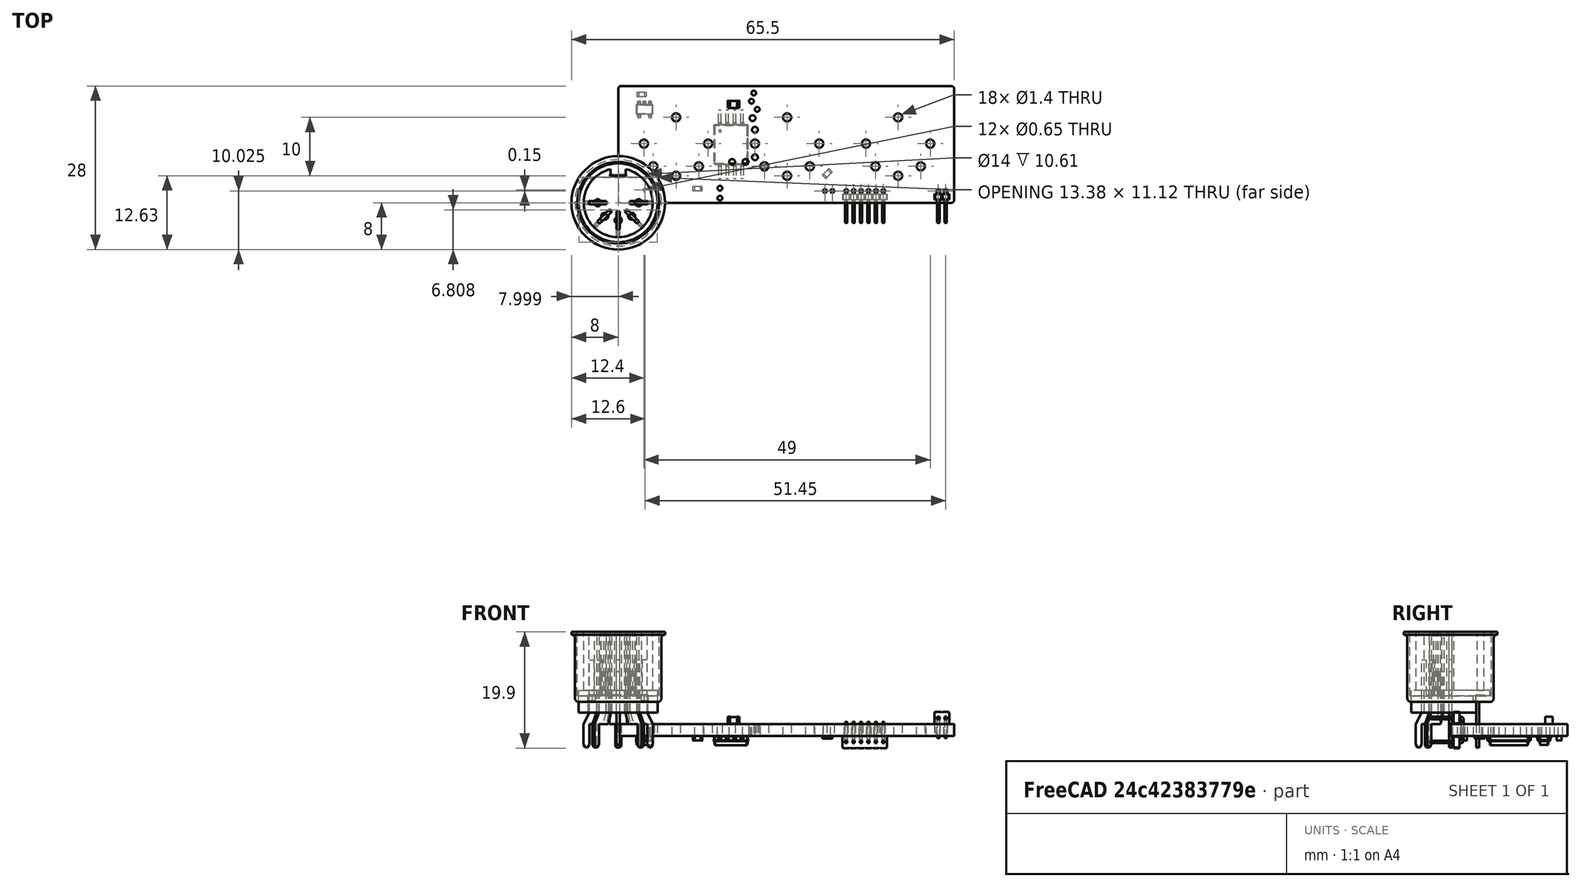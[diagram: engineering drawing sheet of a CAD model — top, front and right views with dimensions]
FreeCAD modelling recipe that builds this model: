
FCSTD DOCUMENT  (FreeCAD 0.20R29177 (Git))
Label: Ultra-midi1
License: All rights reserved
LicenseURL: http://en.wikipedia.org/wiki/All_rights_reserved
objects: Part::Feature×31, App::Link×16, App::Part×8, PartDesign::CoordinateSystem×1, Sketcher::SketchObject×1
note: 33 computed .brp shape members not serialized (recipe doc carries the construction recipe); baked Part::Feature solids carry a one-line shape summary decoded from their .brp

FEATURE [PartDesign::CoordinateSystem] Local_CS_69dd
  AttacherType = Attacher::AttachEngine3D
FEATURE [Part::Feature] Pcb_69dd
  Placement = pos=(-116,98,0) rot=(0,0,1;0rad)
  shape: bbox 57.5 x 20 x 2 mm, 50 faces (baked)
FEATURE [Sketcher::SketchObject] PCB_Sketch_69dd
  FullyConstrained = false
  sketch-geometry (18):
    g0: LineSegment StartX=57 StartY=20 StartZ=0 EndX=0.5 EndY=20 EndZ=0
    g1: LineSegment StartX=8e-16 StartY=19.5 StartZ=0 EndX=0 EndY=0.5 EndZ=0
    g2: LineSegment StartX=57.5 StartY=0.5 StartZ=0 EndX=57.5 EndY=19.5 EndZ=0
    g3: LineSegment StartX=0.5 StartY=0 StartZ=0 EndX=57 EndY=-1.3e-15 EndZ=0
    g4: ArcOfCircle CenterX=57 CenterY=0.500001 CenterZ=0 NormalX=0 NormalY=0 NormalZ=-1 AngleXU=-3.14159 Radius=0.500001 StartAngle=0 EndAngle=1.57079
    g5: ArcOfCircle CenterX=0.500001 CenterY=19.5 CenterZ=0 NormalX=0 NormalY=0 NormalZ=-1 AngleXU=2.66714e-06 Radius=0.500001 StartAngle=0 EndAngle=1.57079
    g6: ArcOfCircle CenterX=0.500001 CenterY=0.500001 CenterZ=0 NormalX=0 NormalY=0 NormalZ=-1 AngleXU=-1.57079 Radius=0.500001 StartAngle=0 EndAngle=1.57079
    g7: ArcOfCircle CenterX=57 CenterY=19.5 CenterZ=0 NormalX=0 NormalY=0 NormalZ=-1 AngleXU=1.5708 Radius=0.500001 StartAngle=0 EndAngle=1.57079
    g8: Circle CenterX=19.5 CenterY=7 CenterZ=0 NormalX=0 NormalY=0 NormalZ=1 AngleXU=0 Radius=0.5
    g9: Circle CenterX=17.4 CenterY=2.5 CenterZ=0 NormalX=0 NormalY=0 NormalZ=1 AngleXU=0 Radius=0.4
    g10: Circle CenterX=23.4 CenterY=7.8 CenterZ=0 NormalX=0 NormalY=0 NormalZ=1 AngleXU=0 Radius=0.5
    g11: Circle CenterX=23.2 CenterY=18.8 CenterZ=0 NormalX=0 NormalY=0 NormalZ=1 AngleXU=0 Radius=0.4
    g12: Circle CenterX=22.8 CenterY=17.4 CenterZ=0 NormalX=0 NormalY=0 NormalZ=1 AngleXU=0 Radius=0.4
    g13: Circle CenterX=23 CenterY=14.5 CenterZ=0 NormalX=0 NormalY=0 NormalZ=1 AngleXU=0 Radius=0.5
    g14: Circle CenterX=23.4 CenterY=12.5 CenterZ=0 NormalX=0 NormalY=0 NormalZ=1 AngleXU=0 Radius=0.5
    g15: Circle CenterX=17.4 CenterY=0.8 CenterZ=0 NormalX=0 NormalY=0 NormalZ=1 AngleXU=0 Radius=0.4
    g16: Circle CenterX=23.8 CenterY=16 CenterZ=0 NormalX=0 NormalY=0 NormalZ=1 AngleXU=0 Radius=0.4
    g17: Circle CenterX=21.8 CenterY=7 CenterZ=0 NormalX=0 NormalY=0 NormalZ=1 AngleXU=0 Radius=0.5
  constraints (8):
    c: Coincident(g1,g6)
    c: Coincident(g1,g5)
    c: Coincident(g3,g6)
    c: Coincident(g0,g5)
    c: Coincident(g3,g4)
    c: Coincident(g0,g7)
    c: Coincident(g2,g4)
    c: Coincident(g2,g7)
FEATURE [Part::Feature] Shape  label="J2_PinHeader_1x02_P127mm_Horizontal_337eb045ee12"
  Placement = pos=(56.05,2.025,0) rot=(0,0,-1;1.5708rad)
  shape: bbox 2.54 x 5.7 x 4.5 mm, 58 faces (baked)
FEATURE [Part::Feature] Shape001  label="C6_C_0805_2012Metric_c09b5ff471bc"
  Placement = pos=(19.75,16.85,0) rot=(0,0,1;0rad)
  shape: bbox 2 x 1.25 x 1.25 mm, 28 faces (baked)
FEATURE [App::Link] J2_PinHeader_1x02_P127mm_Horizontal_337eb045ee12_ln_  label="J3_PinHeader_1x02_P127mm_Horizontal_27ee44c8c3d4"
  LinkPlacement = pos=(36.65,2.025,0) rot=(0,0,-1;1.5708rad)
  LinkedObject = -> Shape
  Placement = pos=(36.65,2.025,0) rot=(0,0,-1;1.5708rad)
FEATURE [Part::Feature] Shape002  label="FB3_L_0603_1608Metric_df2c29076625"
  Placement = pos=(13.6,2.4,-2) rot=(0,1,0;3.14159rad)
  shape: bbox 1.6 x 0.8 x 0.8 mm, 28 faces (baked)
FEATURE [Part::Feature] Shape003  label="C5_C_0603_1608Metric_0867c8c5745e"
  Placement = pos=(4,18.6,-2) rot=(1,0,0;3.14159rad)
  shape: bbox 1.6 x 0.8 x 0.8 mm, 28 faces (baked)
FEATURE [Part::Feature] Shape004  label="R5_R_0603_1608Metric_8c8bab43711c"
  Placement = pos=(35.8,5,-2) rot=(0.92388,0.382683,0;3.14159rad)
  shape: bbox 1.697 x 1.697 x 0.45 mm, 26 faces (baked)
FEATURE [Part::Feature] Shape005  label="J4_PinHeader_1x06_P127mm_Horizontal_489f8f595e1f"
  Placement = pos=(39.025,2.025,-2) rot=(0.707107,-0.707107,0;3.14159rad)
  shape: bbox 7.62 x 5.7 x 4.5 mm, 166 faces (baked)
FEATURE [App::Link] FB3_L_0603_1608Metric_df2c29076625_ln_  label="FB1_L_0603_1608Metric_149065dd4c7b"
  LinkPlacement = pos=(36,7.4,-2) rot=(0.92388,0.382683,0;3.14159rad)
  LinkedObject = -> Shape002
  Placement = pos=(36,7.4,-2) rot=(0.92388,0.382683,0;3.14159rad)
FEATURE [Part::Feature] Shape006  label="U1_SSO_8_68x59mm_P127mm_Clearance8mm_cd01ce0f9bbe"
  Placement = pos=(19.3,10,-2) rot=(0.707107,-0.707107,0;3.14159rad)
  shape: bbox 5.9 x 11.7 x 1.6 mm, 156 faces (baked)
FEATURE [Part::Feature] Shape007  label="U2_SOT_23_5_2942c334eb8a"
  Placement = pos=(4.5,16,-2) rot=(0.707107,-0.707107,0;3.14159rad)
  shape: bbox 2.9 x 2.8 x 1.55 mm, 109 faces (baked)
FEATURE [App::Link] R5_R_0603_1608Metric_8c8bab43711c_ln_  label="R4_R_0603_1608Metric_3ff6b89587b2"
  LinkPlacement = pos=(8,10,-2) rot=(0.707107,0.707107,0;3.14159rad)
  LinkedObject = -> Shape004
  Placement = pos=(8,10,-2) rot=(0.707107,0.707107,0;3.14159rad)
FEATURE [App::Link] C5_C_0603_1608Metric_0867c8c5745e_ln_  label="C2_C_0603_1608Metric_22715801060e"
  LinkPlacement = pos=(10.8,8.2,-2) rot=(1,0,0;3.14159rad)
  LinkedObject = -> Shape003
  Placement = pos=(10.8,8.2,-2) rot=(1,0,0;3.14159rad)
FEATURE [App::Link] C6_C_0805_2012Metric_c09b5ff471bc_ln_  label="C4_C_0805_2012Metric_26a949b8cd84"
  LinkPlacement = pos=(7,12.5,-2) rot=(0,1,0;3.14159rad)
  LinkedObject = -> Shape001
  Placement = pos=(7,12.5,-2) rot=(0,1,0;3.14159rad)
FEATURE [App::Link] R5_R_0603_1608Metric_8c8bab43711c_ln_001  label="R2_R_0603_1608Metric_4e10fd813094"
  LinkPlacement = pos=(49.4,16.5,-2) rot=(0.92388,-0.382683,0;3.14159rad)
  LinkedObject = -> Shape004
  Placement = pos=(49.4,16.5,-2) rot=(0.92388,-0.382683,0;3.14159rad)
FEATURE [App::Link] FB3_L_0603_1608Metric_df2c29076625_ln_001  label="FB2_L_0603_1608Metric_fe7989b07d85"
  LinkPlacement = pos=(12.8,12.2,-2) rot=(0.707107,0.707107,0;3.14159rad)
  LinkedObject = -> Shape002
  Placement = pos=(12.8,12.2,-2) rot=(0.707107,0.707107,0;3.14159rad)
FEATURE [App::Link] C5_C_0603_1608Metric_0867c8c5745e_ln_001  label="C1_C_0603_1608Metric_b41121d6c93c"
  LinkPlacement = pos=(46.1,16.3,-2) rot=(0.92388,0.382683,0;3.14159rad)
  LinkedObject = -> Shape003
  Placement = pos=(46.1,16.3,-2) rot=(0.92388,0.382683,0;3.14159rad)
FEATURE [App::Link] R5_R_0603_1608Metric_8c8bab43711c_ln_002  label="R7_R_0603_1608Metric_dfa80113c302"
  LinkPlacement = pos=(27,1.8,-2) rot=(0,1,0;3.14159rad)
  LinkedObject = -> Shape004
  Placement = pos=(27,1.8,-2) rot=(0,1,0;3.14159rad)
FEATURE [App::Link] FB3_L_0603_1608Metric_df2c29076625_ln_002  label="FB4_L_0603_1608Metric_f99d6db0d256"
  LinkPlacement = pos=(54.15,6.2,-2) rot=(0.707107,-0.707107,0;3.14159rad)
  LinkedObject = -> Shape002
  Placement = pos=(54.15,6.2,-2) rot=(0.707107,-0.707107,0;3.14159rad)
FEATURE [App::Link] FB3_L_0603_1608Metric_df2c29076625_ln_003  label="FB5_L_0603_1608Metric_030844127197"
  LinkPlacement = pos=(25,3.4,-2) rot=(0,1,0;3.14159rad)
  LinkedObject = -> Shape002
  Placement = pos=(25,3.4,-2) rot=(0,1,0;3.14159rad)
FEATURE [App::Link] J2_PinHeader_1x02_P127mm_Horizontal_337eb045ee12_ln_001  label="J1_PinHeader_1x02_P127mm_Horizontal_ae3b6cd6d5c1"
  LinkPlacement = pos=(4.6,2.175,-2) rot=(0.707107,-0.707107,0;3.14159rad)
  LinkedObject = -> Shape
  Placement = pos=(4.6,2.175,-2) rot=(0.707107,-0.707107,0;3.14159rad)
FEATURE [App::Link] R5_R_0603_1608Metric_8c8bab43711c_ln_003  label="R3_R_0603_1608Metric_b0f0240fa3c2"
  LinkPlacement = pos=(14,14.8,-2) rot=(0,1,0;3.14159rad)
  LinkedObject = -> Shape004
  Placement = pos=(14,14.8,-2) rot=(0,1,0;3.14159rad)
FEATURE [App::Link] R5_R_0603_1608Metric_8c8bab43711c_ln_004  label="R6_R_0603_1608Metric_639142cc7455"
  LinkPlacement = pos=(33.2,14.6,-2) rot=(0,1,0;3.14159rad)
  LinkedObject = -> Shape004
  Placement = pos=(33.2,14.6,-2) rot=(0,1,0;3.14159rad)
FEATURE [App::Link] R5_R_0603_1608Metric_8c8bab43711c_ln_005  label="R1_R_0603_1608Metric_cbd55fb59e40"
  LinkPlacement = pos=(53.25,3,-2) rot=(0.707107,0.707107,0;3.14159rad)
  LinkedObject = -> Shape004
  Placement = pos=(53.25,3,-2) rot=(0.707107,0.707107,0;3.14159rad)
FEATURE [App::Link] C5_C_0603_1608Metric_0867c8c5745e_ln_002  label="C3_C_0603_1608Metric_cf41ac51516b"
  LinkPlacement = pos=(33.1375,16.2,-2) rot=(1,0,0;3.14159rad)
  LinkedObject = -> Shape003
  Placement = pos=(33.1375,16.2,-2) rot=(1,0,0;3.14159rad)
FEATURE [App::Part] Bot_69dd
  Group = -> [Shape002,Shape003,Shape004,Shape005,FB3_L_0603_1608Metric_df2c29076625_ln_,Shape006,Shape007,R5_R_0603_1608Metric_8c8bab43711c_ln_,C5_C_0603_1608Metric_0867c8c5745e_ln_,C6_C_0805_2012Metric_c09b5ff471bc_ln_,R5_R_0603_1608Metric_8c8bab43711c_ln_001,FB3_L_0603_1608Metric_df2c29076625_ln_001,C5_C_0603_1608Metric_0867c8c5745e_ln_001,R5_R_0603_1608Metric_8c8bab43711c_ln_002,+7 more]
  Origin = -> Origin004
FEATURE [Part::Feature] Part__Feature  label="Casing"
  shape: bbox 18.09 x 18.09 x 19.8 mm, 30 faces (baked)
FEATURE [Part::Feature] Part__Feature001  label="Plastic"
  Placement = pos=(0,0,0) rot=(0,0,1;1.5708rad)
  shape: bbox 13.5 x 13.5 x 13.8 mm, 83 faces (baked)
FEATURE [Part::Feature] Part__Feature002  label="Pin-contact1"
  Placement = pos=(0,0,-4) rot=(0,0,1;0rad)
  shape: bbox 3.9 x 0.55 x 15 mm, 20 faces (baked)
FEATURE [Part::Feature] Part__Feature003  label="Pin-contact002"
  Placement = pos=(0,0,-4) rot=(0,0,1;1.5708rad)
  shape: bbox 0.55 x 3.9 x 15 mm, 20 faces (baked)
FEATURE [Part::Feature] Part__Feature004  label="Pin-contact003"
  Placement = pos=(0,0,-4) rot=(0,0,1;3.14159rad)
  shape: bbox 3.9 x 0.55 x 15 mm, 20 faces (baked)
FEATURE [Part::Feature] Part__Feature005  label="Pin-contact004"
  Placement = pos=(0,0,-4) rot=(0,0,1;0.785398rad)
  shape: bbox 3.147 x 3.147 x 15 mm, 20 faces (baked)
FEATURE [Part::Feature] Part__Feature006  label="Pin-contact005"
  Placement = pos=(0,0,-4) rot=(0,0,1;2.35619rad)
  shape: bbox 3.147 x 3.147 x 15 mm, 20 faces (baked)
FEATURE [App::Part] CUI_SD_50BV
  Group = -> [Part__Feature,Part__Feature001,Part__Feature002,Part__Feature003,Part__Feature004,Part__Feature005,Part__Feature006]
  Origin = -> Origin005
  Placement = pos=(9.9,10.15,0) rot=(0,0,1;0rad)
FEATURE [Part::Feature] Part__Feature007  label="Casing001"
  shape: bbox 18.09 x 18.09 x 19.8 mm, 30 faces (baked)
FEATURE [Part::Feature] Part__Feature008  label="Plastic001"
  Placement = pos=(0,0,0) rot=(0,0,1;1.5708rad)
  shape: bbox 13.5 x 13.5 x 13.8 mm, 83 faces (baked)
FEATURE [Part::Feature] Part__Feature009  label="Pin-contact006"
  Placement = pos=(0,0,-4) rot=(0,0,1;0rad)
  shape: bbox 3.9 x 0.55 x 15 mm, 20 faces (baked)
FEATURE [Part::Feature] Part__Feature010  label="Pin-contact007"
  Placement = pos=(0,0,-4) rot=(0,0,1;1.5708rad)
  shape: bbox 0.55 x 3.9 x 15 mm, 20 faces (baked)
FEATURE [Part::Feature] Part__Feature011  label="Pin-contact008"
  Placement = pos=(0,0,-4) rot=(0,0,1;3.14159rad)
  shape: bbox 3.9 x 0.55 x 15 mm, 20 faces (baked)
FEATURE [Part::Feature] Part__Feature012  label="Pin-contact009"
  Placement = pos=(0,0,-4) rot=(0,0,1;0.785398rad)
  shape: bbox 3.147 x 3.147 x 15 mm, 20 faces (baked)
FEATURE [Part::Feature] Part__Feature013  label="Pin-contact010"
  Placement = pos=(0,0,-4) rot=(0,0,1;2.35619rad)
  shape: bbox 3.147 x 3.147 x 15 mm, 20 faces (baked)
FEATURE [App::Part] CUI_SD_50BV001
  Group = -> [Part__Feature007,Part__Feature008,Part__Feature009,Part__Feature010,Part__Feature011,Part__Feature012,Part__Feature013]
  Origin = -> Origin006
  Placement = pos=(28.9,10.15,0) rot=(0,0,1;0rad)
FEATURE [Part::Feature] Part__Feature014  label="Casing002"
  shape: bbox 18.09 x 18.09 x 19.8 mm, 30 faces (baked)
FEATURE [Part::Feature] Part__Feature015  label="Plastic002"
  Placement = pos=(0,0,0) rot=(0,0,1;1.5708rad)
  shape: bbox 13.5 x 13.5 x 13.8 mm, 83 faces (baked)
FEATURE [Part::Feature] Part__Feature016  label="Pin-contact011"
  Placement = pos=(0,0,-4) rot=(0,0,1;0rad)
  shape: bbox 3.9 x 0.55 x 15 mm, 20 faces (baked)
FEATURE [Part::Feature] Part__Feature017  label="Pin-contact012"
  Placement = pos=(0,0,-4) rot=(0,0,1;1.5708rad)
  shape: bbox 0.55 x 3.9 x 15 mm, 20 faces (baked)
FEATURE [Part::Feature] Part__Feature018  label="Pin-contact013"
  Placement = pos=(0,0,-4) rot=(0,0,1;3.14159rad)
  shape: bbox 3.9 x 0.55 x 15 mm, 20 faces (baked)
FEATURE [Part::Feature] Part__Feature019  label="Pin-contact014"
  Placement = pos=(0,0,-4) rot=(0,0,1;0.785398rad)
  shape: bbox 3.147 x 3.147 x 15 mm, 20 faces (baked)
FEATURE [Part::Feature] Part__Feature020  label="Pin-contact015"
  Placement = pos=(0,0,-4) rot=(0,0,1;2.35619rad)
  shape: bbox 3.147 x 3.147 x 15 mm, 20 faces (baked)
FEATURE [App::Part] CUI_SD_50BV002
  Group = -> [Part__Feature014,Part__Feature015,Part__Feature016,Part__Feature017,Part__Feature018,Part__Feature019,Part__Feature020]
  Origin = -> Origin007
  Placement = pos=(47.9,10.15,0) rot=(0,0,1;0rad)
FEATURE [App::Part] Top_69dd
  Group = -> [Shape,Shape001,J2_PinHeader_1x02_P127mm_Horizontal_337eb045ee12_ln_,CUI_SD_50BV,CUI_SD_50BV001,CUI_SD_50BV002]
  Origin = -> Origin003
FEATURE [App::Part] Step_Models_69dd
  Group = -> [Top_69dd,Bot_69dd]
  Origin = -> Origin002
FEATURE [Part::Feature] pads_area009001  label="topPads_69dd"
  Placement = pos=(-116,98,0.02) rot=(0,0,1;0rad)
  shape: bbox 54.45 x 16.58 x 2e-07 mm, 46 faces, 0 solids (baked)
FEATURE [App::Part] Board_Geoms_69dd
  Group = -> [Local_CS_69dd,Pcb_69dd,pads_area009001,PCB_Sketch_69dd]
  Origin = -> Origin
FEATURE [App::Part] Board_69dd  label="Ultra-Midi"
  Group = -> [Board_Geoms_69dd,Step_Models_69dd]
  Origin = -> Origin001
